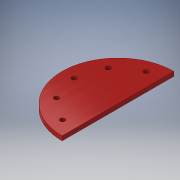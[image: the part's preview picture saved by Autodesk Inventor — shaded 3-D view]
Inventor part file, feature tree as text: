
AUTODESK INVENTOR PART (.ipt)
format: ipt  version: 2019 (Build 230136000, 136)  size: 118,272 bytes
history: native  units: in
note: dims shown in document units (in); Inventor stores cm internally (conversion verified against a paired STEP export)
features: extrude x3, sketch x3
ambient origin geometry x8: Origin, YZ Plane, XZ Plane, XY Plane, X Axis, Y Axis, Z Axis, Center Point
bodies: Solid1 (feature_tree)
feature tree (6):
  extrude  "Extrusion1"  Depth=0.25in TaperAngle=0.0deg
  extrude  "Extrusion2"  Depth=5.0in
  extrude  "Extrusion3"  Depth=3.937in TaperAngle=360.0deg
  sketch  "Sketch1"  dims[d0=0.25in d1=0.0in d2=0.25in d3=0.0in]
  sketch  "Sketch2"  dims[d4=6.35in d17=5.0in]
  sketch  "Sketch5"  dims[d18=0.266in d19=3.937in d21=360.0deg d23=0.0in d24=0.0in]
